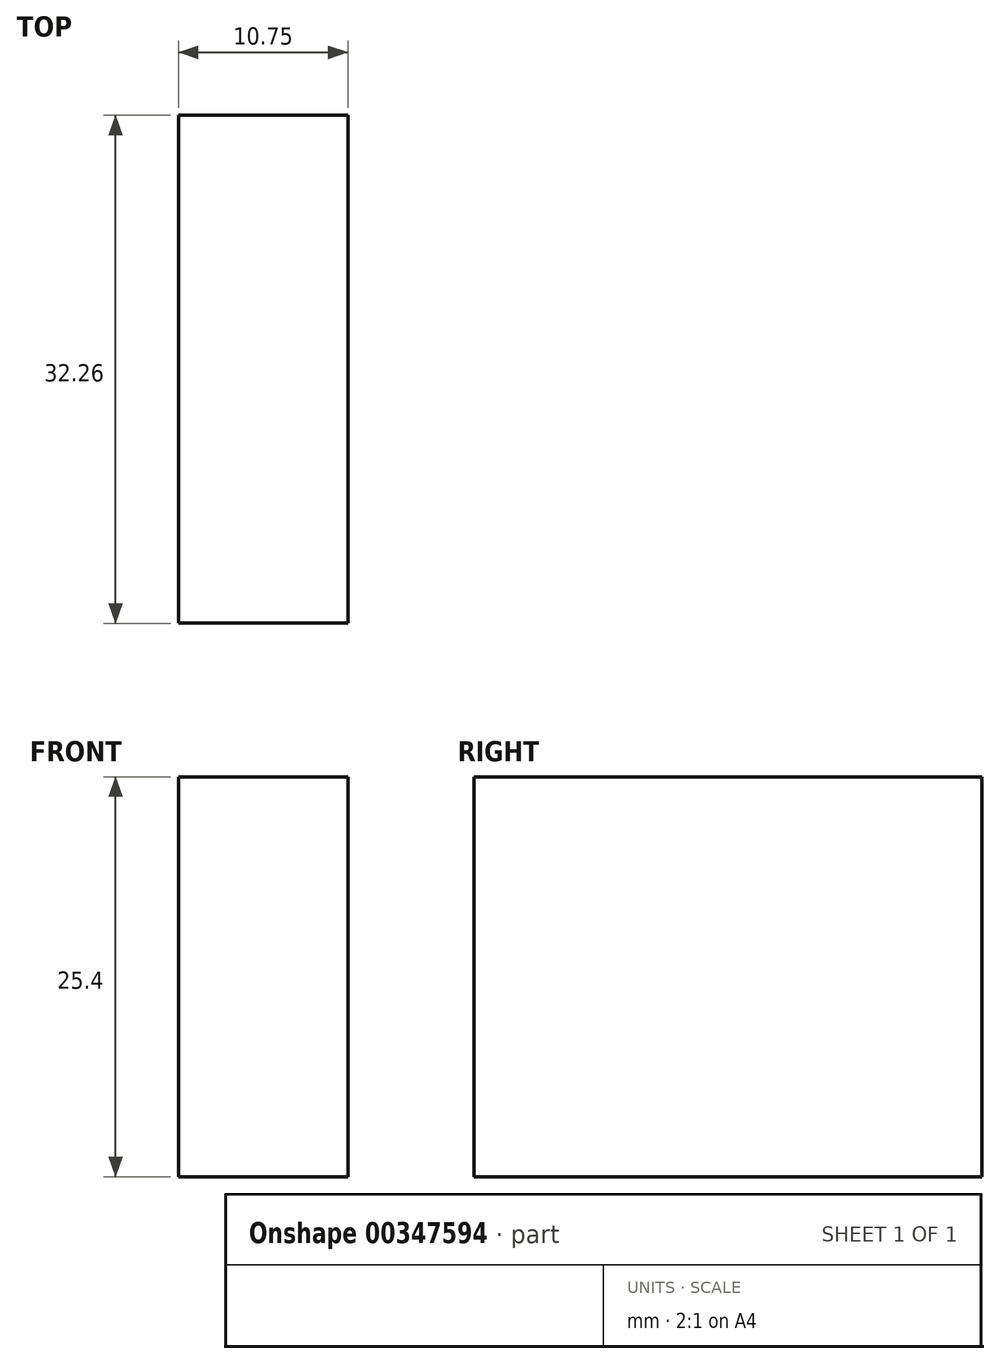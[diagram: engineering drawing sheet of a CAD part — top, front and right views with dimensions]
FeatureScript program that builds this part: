
annotation { "Feature Type Name" : "Feature", "Feature Type Description" : "" }
export const myFeature = defineFeature(function(context is Context, id is Id, definition is map)
    precondition{}
    {
        {
            var Q0;
            Q0=qCreatedBy(makeId("Top.planeOp"),FACE);
            var sketch = newSketch(context, id + "F0", { "sketchPlane" : qUnion([Q0])});
            skLineSegment(sketch, "E0.bottom", {"start": v(-48.4, 45.7) * mm, "end": v(-37.64, 45.7) * mm});
            skLineSegment(sketch, "E0.top", {"start": v(-48.4, 13.44) * mm, "end": v(-37.64, 13.44) * mm});
            skLineSegment(sketch, "E0.left", {"start": v(-48.4, 45.7) * mm, "end": v(-48.4, 13.44) * mm});
            skLineSegment(sketch, "E0.right", {"start": v(-37.64, 45.7) * mm, "end": v(-37.64, 13.44) * mm});
            skSolve(sketch);
        }
        {
            var Q0;
            Q0=makeQuery(id+"F0.imprint","IMPRINT",FACE,{"disambiguationData":[TD([[makeQuery(id+"F0.imprint","IMPRINT",EDGE,{"derivedFrom":sQuery(id+"F0.wireOp",EDGE,"E0.bottom")}),-1.0]])]});
            extrude(context, id + "F1", {"entities" : qUnion([Q0]), "depth" : 25.4 * mm});
        }
    });
